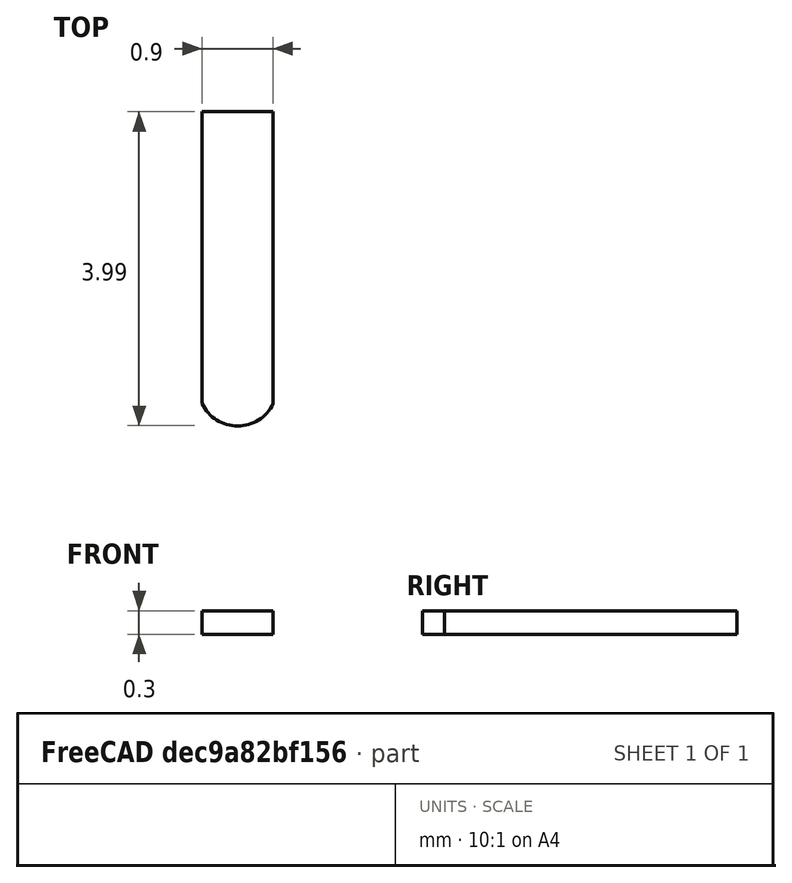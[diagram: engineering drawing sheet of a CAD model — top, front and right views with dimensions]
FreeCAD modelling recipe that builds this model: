
FCSTD DOCUMENT  (FreeCAD 0.19R16699 (Git))
Label: RD902F_Terminal_Type_20
License: All rights reserved
LicenseURL: http://en.wikipedia.org/wiki/All_rights_reserved
objects: Sketcher::SketchObject×1, PartDesign::Pad×1, PartDesign::Body×1, App::Part×1
note: 4 computed .brp shape members not serialized (recipe doc carries the construction recipe); baked Part::Feature solids carry a one-line shape summary decoded from their .brp

FEATURE [Sketcher::SketchObject] Sketch
  MapMode = 5
  Support = -> [XY_Plane]
  sketch-geometry (7):
    g0: ArcOfCircle CenterX=0 CenterY=-3.49746 CenterZ=0 NormalX=0 NormalY=0 NormalZ=1 AngleXU=0 Radius=0.497458 StartAngle=3.58195 EndAngle=5.84283
    g1: LineSegment StartX=-0.45 StartY=-3.70951 StartZ=0 EndX=-0.45 EndY=0 EndZ=0
    g2: LineSegment StartX=0.45 StartY=-3.70951 StartZ=0 EndX=0.45 EndY=0 EndZ=0
    g3: LineSegment StartX=-0.45 StartY=0 StartZ=0 EndX=0.45 EndY=0 EndZ=0
    g4: LineSegment [constr] StartX=0.45 StartY=-3.70951 StartZ=0 EndX=-0.45 EndY=-3.70951 EndZ=0
    g5: GeomPoint X=0 Y=-3 Z=0
    g6: LineSegment [constr] StartX=0 StartY=-3 StartZ=0 EndX=0 EndY=-3.49746 EndZ=0
  constraints (18):
    c: PointOnObject(g0,g-2)
    c: Coincident(g1,g0)
    c: PointOnObject(g1,g-1)
    c: Vertical(g1)
    c: Coincident(g2,g0)
    c: PointOnObject(g2,g-1)
    c: Vertical(g2)
    c: Coincident(g3,g1)
    c: Coincident(g3,g2)
    c: Coincident(g4,g0)
    c: Coincident(g4,g0)
    c: Horizontal(g4)
    c: DistanceX(g3,g3) = 0.9
    c: PointOnObject(g5,g0)
    c: Coincident(g6,g5)
    c: Coincident(g6,g0)
    c: PointOnObject(g5,g-2)
    c: DistanceY(g5,g-1) = 3
FEATURE [PartDesign::Pad] Pad
  Length = 0.3
  Length2 = 100
  Midplane = true
  Profile = -> Sketch
  Type = 0
FEATURE [PartDesign::Body] Body  label="RD901F_Terminal_Type_20_1"
  Group = -> [Sketch,Pad]
  Origin = -> Origin
  Tip = -> Pad
FEATURE [App::Part] Part  label="RD902F_Terminal_Type_20"
  Group = -> [Body]
  Origin = -> Origin001
